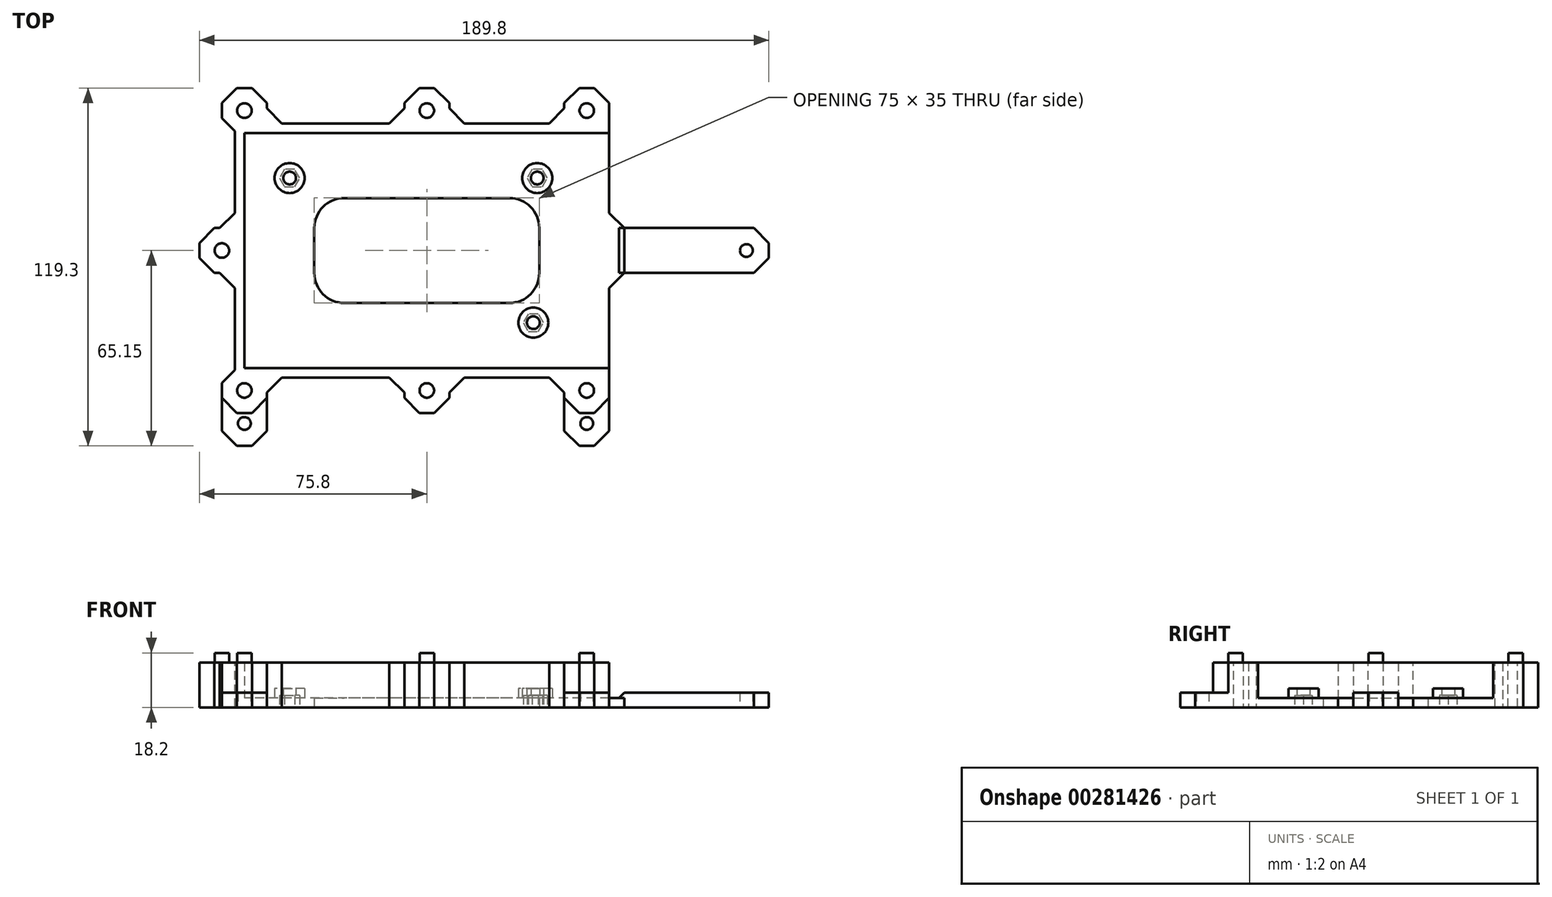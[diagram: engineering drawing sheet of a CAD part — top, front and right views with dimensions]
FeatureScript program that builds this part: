
annotation { "Feature Type Name" : "Feature", "Feature Type Description" : "" }
export const myFeature = defineFeature(function(context is Context, id is Id, definition is map)
    precondition{}
    {
        {
            var Q0;
            Q0=qCreatedBy(makeId("Top.planeOp"),FACE);
            var sketch = newSketch(context, id + "F0", { "sketchPlane" : qUnion([Q0])});
            skLineSegment(sketch, "E0.rect.bottom", {"start": v(50.8, -26.65) * mm, "end": v(-50.8, -26.65) * mm, "construction": true});
            skLineSegment(sketch, "E0.rect.top", {"start": v(50.8, 26.65) * mm, "end": v(-50.8, 26.65) * mm, "construction": true});
            skLineSegment(sketch, "E0.rect.left", {"start": v(50.8, -26.65) * mm, "end": v(50.8, 26.65) * mm, "construction": true});
            skLineSegment(sketch, "E0.rect.right", {"start": v(-50.8, -26.65) * mm, "end": v(-50.8, 26.65) * mm, "construction": true});
            skPoint(sketch, "E0.rect.middle", {"position": v(0, 0) * mm});
            skCircle(sketch, "E1", {"center": v(36.8, 24.15) * mm, "radius": 2.12 * mm});
            skCircle(sketch, "E2", {"center": v(-45.72, 24.15) * mm, "radius": 2.12 * mm});
            skLineSegment(sketch, "E3.rect.bottom", {"start": v(60.8, -39.15) * mm, "end": v(-60.8, -39.15) * mm});
            skLineSegment(sketch, "E3.rect.top", {"start": v(60.8, 39.15) * mm, "end": v(-60.8, 39.15) * mm});
            skLineSegment(sketch, "E3.rect.left", {"start": v(60.8, -39.15) * mm, "end": v(60.8, 39.15) * mm});
            skLineSegment(sketch, "E3.rect.right", {"start": v(-60.8, -39.15) * mm, "end": v(-60.8, 39.15) * mm});
            skLineSegment(sketch, "E4.rect.bottom", {"start": v(27.5, -17.5) * mm, "end": v(-27.5, -17.5) * mm});
            skLineSegment(sketch, "E4.rect.top", {"start": v(27.5, 17.5) * mm, "end": v(-27.5, 17.5) * mm});
            skLineSegment(sketch, "E4.rect.left", {"start": v(37.5, -7.5) * mm, "end": v(37.5, 7.5) * mm});
            skLineSegment(sketch, "E4.rect.right", {"start": v(-37.5, -7.5) * mm, "end": v(-37.5, 7.5) * mm});
            skPoint(sketch, "E5.visualSharp", {"position": v(-37.5, 17.5) * mm});
            skArc(sketch, "E5.filletArc", {"start": v(-27.5, 17.5) * mm, "mid": v(-34.57, 14.57) * mm, "end": v(-37.5, 7.5) * mm});
            skPoint(sketch, "E6.visualSharp", {"position": v(-37.5, -17.5) * mm});
            skArc(sketch, "E6.filletArc", {"start": v(-37.5, -7.5) * mm, "mid": v(-34.57, -14.57) * mm, "end": v(-27.5, -17.5) * mm});
            skPoint(sketch, "E7.visualSharp", {"position": v(37.5, -17.5) * mm});
            skArc(sketch, "E7.filletArc", {"start": v(27.5, -17.5) * mm, "mid": v(34.57, -14.57) * mm, "end": v(37.5, -7.5) * mm});
            skPoint(sketch, "E8.visualSharp", {"position": v(37.5, 17.5) * mm});
            skArc(sketch, "E8.filletArc", {"start": v(37.5, 7.5) * mm, "mid": v(34.57, 14.57) * mm, "end": v(27.5, 17.5) * mm});
            skCircle(sketch, "E9", {"center": v(35.5, -24.05) * mm, "radius": 2.12 * mm});
            skSolve(sketch);
        }
        {
            var Q0;
            Q0=qSketchRegion(id+"F0",true);
            extrude(context, id + "F1", {"entities" : qUnion([Q0]), "depth" : 3.2 * mm});
        }
        {
            var Q0;
            Q0=makeQuery(id+"F1.opExtrude","CAP_FACE",FACE,{"disambiguationData":[OSD([sQuery(id+"F0.wireOp",EDGE,"E1"),sQuery(id+"F0.wireOp",EDGE,"E2"),sQuery(id+"F0.wireOp",EDGE,"427397f8-0dd3-485f-8eed-9c75a59d67ec"),sQuery(id+"F0.wireOp",EDGE,"E3.rect.bottom"),sQuery(id+"F0.wireOp",EDGE,"E3.rect.top"),sQuery(id+"F0.wireOp",EDGE,"E3.rect.left"),sQuery(id+"F0.wireOp",EDGE,"E3.rect.right"),sQuery(id+"F0.wireOp",EDGE,"E4.rect.bottom"),sQuery(id+"F0.wireOp",EDGE,"E4.rect.top"),sQuery(id+"F0.wireOp",EDGE,"E4.rect.left"),sQuery(id+"F0.wireOp",EDGE,"E4.rect.right")])],"isStart":false});
            var sketch = newSketch(context, id + "F2", { "sketchPlane" : qUnion([Q0])});
            skCircle(sketch, "E10", {"center": v(-45.72, 24.15) * mm, "radius": 5 * mm});
            skCircle(sketch, "E11", {"center": v(36.8, 24.15) * mm, "radius": 5 * mm});
            skCircle(sketch, "E12", {"center": v(-45.72, 24.15) * mm, "radius": 2.12 * mm});
            skCircle(sketch, "E13", {"center": v(36.8, 24.15) * mm, "radius": 2.12 * mm});
            skLineSegment(sketch, "E14", {"start": v(0, 0) * mm, "end": v(17.05, 0) * mm, "construction": true});
            skCircle(sketch, "E15", {"center": v(35.5, -24.05) * mm, "radius": 5 * mm});
            skCircle(sketch, "E16", {"center": v(35.5, -24.05) * mm, "radius": 2.12 * mm});
            skSolve(sketch);
        }
        {
            var Q0;
            Q0=qSketchRegion(id+"F2",true);
            extrude(context, id + "F3", {"entities" : qUnion([Q0]), "operationType" : NewBodyOperationType.ADD, "depth" : 3.2 * mm});
        }
        {
            var Q0;
            Q0=makeQuery(id+"F1.opExtrude","CAP_FACE",FACE,{"disambiguationData":[OSD([sQuery(id+"F0.wireOp",EDGE,"E1"),sQuery(id+"F0.wireOp",EDGE,"E2"),sQuery(id+"F0.wireOp",EDGE,"427397f8-0dd3-485f-8eed-9c75a59d67ec"),sQuery(id+"F0.wireOp",EDGE,"E3.rect.bottom"),sQuery(id+"F0.wireOp",EDGE,"E3.rect.top"),sQuery(id+"F0.wireOp",EDGE,"E3.rect.left"),sQuery(id+"F0.wireOp",EDGE,"E3.rect.right"),sQuery(id+"F0.wireOp",EDGE,"E4.rect.bottom"),sQuery(id+"F0.wireOp",EDGE,"E4.rect.top"),sQuery(id+"F0.wireOp",EDGE,"E4.rect.left"),sQuery(id+"F0.wireOp",EDGE,"E4.rect.right")])],"isStart":true});
            var sketch = newSketch(context, id + "F4", { "sketchPlane" : qUnion([Q0])});
            skCircle(sketch, "E17.cCircle", {"center": v(-45.72, -24.15) * mm, "radius": 2.93 * mm, "construction": true});
            skLineSegment(sketch, "E17.0", {"start": v(-47.4, -21.23) * mm, "end": v(-44.03, -21.23) * mm});
            skLineSegment(sketch, "E17.1", {"start": v(-44.03, -21.23) * mm, "end": v(-42.34, -24.15) * mm});
            skLineSegment(sketch, "E17.2", {"start": v(-42.34, -24.15) * mm, "end": v(-44.03, -27.08) * mm});
            skLineSegment(sketch, "E17.3", {"start": v(-44.03, -27.08) * mm, "end": v(-47.4, -27.08) * mm});
            skLineSegment(sketch, "E17.4", {"start": v(-47.4, -27.08) * mm, "end": v(-49.1, -24.15) * mm});
            skLineSegment(sketch, "E17.5", {"start": v(-49.1, -24.15) * mm, "end": v(-47.4, -21.23) * mm});
            skPoint(sketch, "E17.0.midPoint", {"position": v(-45.72, -21.23) * mm});
            skCircle(sketch, "E18.cCircle", {"center": v(36.8, -24.15) * mm, "radius": 2.93 * mm, "construction": true});
            skLineSegment(sketch, "E18.0", {"start": v(35.11, -21.22) * mm, "end": v(38.49, -21.22) * mm});
            skLineSegment(sketch, "E18.1", {"start": v(38.49, -21.22) * mm, "end": v(40.18, -24.15) * mm});
            skLineSegment(sketch, "E18.2", {"start": v(40.18, -24.15) * mm, "end": v(38.49, -27.08) * mm});
            skLineSegment(sketch, "E18.3", {"start": v(38.49, -27.07) * mm, "end": v(35.11, -27.07) * mm});
            skLineSegment(sketch, "E18.4", {"start": v(35.11, -27.08) * mm, "end": v(33.42, -24.15) * mm});
            skLineSegment(sketch, "E18.5", {"start": v(33.42, -24.15) * mm, "end": v(35.11, -21.22) * mm});
            skPoint(sketch, "E18.0.midPoint", {"position": v(36.8, -21.23) * mm});
            skCircle(sketch, "E19.cCircle", {"center": v(35.5, 24.05) * mm, "radius": 2.93 * mm, "construction": true});
            skLineSegment(sketch, "E19.0", {"start": v(37.19, 21.12) * mm, "end": v(33.81, 21.12) * mm});
            skLineSegment(sketch, "E19.1", {"start": v(33.81, 21.12) * mm, "end": v(32.12, 24.05) * mm});
            skLineSegment(sketch, "E19.2", {"start": v(32.12, 24.05) * mm, "end": v(33.81, 26.97) * mm});
            skLineSegment(sketch, "E19.3", {"start": v(33.81, 26.97) * mm, "end": v(37.19, 26.97) * mm});
            skLineSegment(sketch, "E19.4", {"start": v(37.19, 26.97) * mm, "end": v(38.88, 24.05) * mm});
            skLineSegment(sketch, "E19.5", {"start": v(38.88, 24.05) * mm, "end": v(37.19, 21.12) * mm});
            skPoint(sketch, "E19.0.midPoint", {"position": v(35.5, 21.12) * mm});
            skSolve(sketch);
        }
        {
            var Q0;
            Q0=qSketchRegion(id+"F4",true);
            extrude(context, id + "F5", {"entities" : qUnion([Q0]), "operationType" : NewBodyOperationType.REMOVE, "oppositeDirection" : true, "depth" : 4 * mm});
        }
        {
            var Q0;
            Q0=qCreatedBy(makeId("Top.planeOp"),FACE);
            var sketch = newSketch(context, id + "F6", { "sketchPlane" : qUnion([Q0])});
            skLineSegment(sketch, "E20", {"start": v(60.8, 39.15) * mm, "end": v(-60.8, 39.15) * mm});
            skLineSegment(sketch, "E21", {"start": v(-60.8, 39.15) * mm, "end": v(-60.8, -39.15) * mm});
            skLineSegment(sketch, "E22", {"start": v(-60.8, -39.15) * mm, "end": v(60.8, -39.15) * mm});
            skLineSegment(sketch, "E23", {"start": v(60.8, -39.15) * mm, "end": v(60.8, -54.15) * mm});
            skLineSegment(sketch, "E24", {"start": v(60.8, -54.15) * mm, "end": v(45.8, -54.15) * mm});
            skLineSegment(sketch, "E25", {"start": v(45.8, -54.15) * mm, "end": v(45.8, -42.35) * mm});
            skLineSegment(sketch, "E26", {"start": v(45.8, -42.35) * mm, "end": v(7.5, -42.35) * mm});
            skLineSegment(sketch, "E27", {"start": v(7.5, -42.35) * mm, "end": v(7.5, -54.15) * mm});
            skLineSegment(sketch, "E28", {"start": v(7.5, -54.15) * mm, "end": v(-7.5, -54.15) * mm});
            skLineSegment(sketch, "E29", {"start": v(-7.5, -54.15) * mm, "end": v(-7.5, -42.35) * mm});
            skLineSegment(sketch, "E30", {"start": v(-7.5, -42.35) * mm, "end": v(-53.3, -42.35) * mm});
            skLineSegment(sketch, "E31", {"start": v(-53.3, -42.35) * mm, "end": v(-53.3, -54.15) * mm});
            skLineSegment(sketch, "E32", {"start": v(-53.3, -54.15) * mm, "end": v(-68.3, -54.15) * mm});
            skLineSegment(sketch, "E33", {"start": v(-68.3, -54.15) * mm, "end": v(-68.3, -39.15) * mm});
            skLineSegment(sketch, "E34", {"start": v(-68.3, -39.15) * mm, "end": v(-64, -39.15) * mm});
            skLineSegment(sketch, "E35", {"start": v(-64, -39.15) * mm, "end": v(-64, -7.5) * mm});
            skLineSegment(sketch, "E36", {"start": v(-64, -7.5) * mm, "end": v(-75.8, -7.5) * mm});
            skLineSegment(sketch, "E37", {"start": v(-75.8, -7.5) * mm, "end": v(-75.8, 7.5) * mm});
            skLineSegment(sketch, "E38", {"start": v(-75.8, 7.5) * mm, "end": v(-64, 7.5) * mm});
            skLineSegment(sketch, "E39", {"start": v(-64, 7.5) * mm, "end": v(-64, 39.15) * mm});
            skLineSegment(sketch, "E40", {"start": v(-64, 39.15) * mm, "end": v(-68.3, 39.15) * mm});
            skLineSegment(sketch, "E41", {"start": v(-68.3, 39.15) * mm, "end": v(-68.3, 54.15) * mm});
            skLineSegment(sketch, "E42", {"start": v(-68.3, 54.15) * mm, "end": v(-53.3, 54.15) * mm});
            skLineSegment(sketch, "E43", {"start": v(-53.3, 54.15) * mm, "end": v(-53.3, 42.35) * mm});
            skLineSegment(sketch, "E44", {"start": v(-53.3, 42.35) * mm, "end": v(-7.5, 42.35) * mm});
            skLineSegment(sketch, "E45", {"start": v(-7.5, 42.35) * mm, "end": v(-7.5, 54.15) * mm});
            skLineSegment(sketch, "E46", {"start": v(-7.5, 54.15) * mm, "end": v(7.5, 54.15) * mm});
            skLineSegment(sketch, "E47", {"start": v(7.5, 54.15) * mm, "end": v(7.5, 42.35) * mm});
            skLineSegment(sketch, "E48", {"start": v(7.5, 42.35) * mm, "end": v(45.8, 42.35) * mm});
            skLineSegment(sketch, "E49", {"start": v(45.8, 42.35) * mm, "end": v(45.8, 54.15) * mm});
            skLineSegment(sketch, "E50", {"start": v(45.8, 54.15) * mm, "end": v(60.8, 54.15) * mm});
            skLineSegment(sketch, "E51", {"start": v(60.8, 54.15) * mm, "end": v(60.8, 39.15) * mm});
            skSolve(sketch);
        }
        {
            var Q0;
            Q0=qSketchRegion(id+"F6",true);
            extrude(context, id + "F7", {"entities" : qUnion([Q0]), "operationType" : NewBodyOperationType.ADD, "depth" : 15 * mm});
        }
        {
            var Q0;
            Q0=makeQuery(id+"F7.opExtrude","CAP_FACE",FACE,{"disambiguationData":[OSD([sQuery(id+"F6.wireOp",EDGE,"E20"),sQuery(id+"F6.wireOp",EDGE,"E21"),sQuery(id+"F6.wireOp",EDGE,"E22"),sQuery(id+"F6.wireOp",EDGE,"E23"),sQuery(id+"F6.wireOp",EDGE,"E24"),sQuery(id+"F6.wireOp",EDGE,"E25"),sQuery(id+"F6.wireOp",EDGE,"E26"),sQuery(id+"F6.wireOp",EDGE,"E27"),sQuery(id+"F6.wireOp",EDGE,"E28"),sQuery(id+"F6.wireOp",EDGE,"E29"),sQuery(id+"F6.wireOp",EDGE,"E30"),sQuery(id+"F6.wireOp",EDGE,"E31"),sQuery(id+"F6.wireOp",EDGE,"E32"),sQuery(id+"F6.wireOp",EDGE,"E33"),sQuery(id+"F6.wireOp",EDGE,"E34"),sQuery(id+"F6.wireOp",EDGE,"E35"),sQuery(id+"F6.wireOp",EDGE,"E36"),sQuery(id+"F6.wireOp",EDGE,"E37"),sQuery(id+"F6.wireOp",EDGE,"E38"),sQuery(id+"F6.wireOp",EDGE,"E39"),sQuery(id+"F6.wireOp",EDGE,"E40"),sQuery(id+"F6.wireOp",EDGE,"E41"),sQuery(id+"F6.wireOp",EDGE,"E42"),sQuery(id+"F6.wireOp",EDGE,"E43"),sQuery(id+"F6.wireOp",EDGE,"E44"),sQuery(id+"F6.wireOp",EDGE,"E45"),sQuery(id+"F6.wireOp",EDGE,"E46"),sQuery(id+"F6.wireOp",EDGE,"E47"),sQuery(id+"F6.wireOp",EDGE,"E48"),sQuery(id+"F6.wireOp",EDGE,"E49"),sQuery(id+"F6.wireOp",EDGE,"E50"),sQuery(id+"F6.wireOp",EDGE,"E51")])],"isStart":false});
            var sketch = newSketch(context, id + "F8", { "sketchPlane" : qUnion([Q0])});
            skCircle(sketch, "E52", {"center": v(53.3, 46.65) * mm, "radius": 2.43 * mm});
            skCircle(sketch, "E53", {"center": v(0, 46.65) * mm, "radius": 2.43 * mm});
            skCircle(sketch, "E54", {"center": v(-60.8, 46.65) * mm, "radius": 2.43 * mm});
            skCircle(sketch, "E55", {"center": v(-68.3, 0) * mm, "radius": 2.43 * mm});
            skLineSegment(sketch, "E56", {"start": v(0, 0) * mm, "end": v(61.66, 0) * mm, "construction": true});
            skCircle(sketch, "E57.MirrorC", {"center": v(-60.8, -46.65) * mm, "radius": 2.43 * mm});
            skCircle(sketch, "E58.MirrorC", {"center": v(0, -46.65) * mm, "radius": 2.43 * mm});
            skCircle(sketch, "E59.MirrorC", {"center": v(53.3, -46.65) * mm, "radius": 2.43 * mm});
            skSolve(sketch);
        }
        {
            var Q0;
            Q0=qSketchRegion(id+"F8",true);
            extrude(context, id + "F9", {"entities" : qUnion([Q0]), "operationType" : NewBodyOperationType.ADD, "depth" : 3.2 * mm});
        }
        {
            var Q0;
            Q0=makeQuery(id+"F7.opExtrude","SWEPT_EDGE",EDGE,{"disambiguationData":[OSD([sQuery(id+"F6.wireOp",EDGE,"E36"),sQuery(id+"F6.wireOp",EDGE,"E37")])]});
            var Q1;
            Q1=makeQuery(id+"F7.opExtrude","SWEPT_EDGE",EDGE,{"disambiguationData":[OSD([sQuery(id+"F6.wireOp",EDGE,"E37"),sQuery(id+"F6.wireOp",EDGE,"E38")])]});
            var Q2;
            Q2=makeQuery(id+"F7.opExtrude","SWEPT_EDGE",EDGE,{"disambiguationData":[OSD([sQuery(id+"F6.wireOp",EDGE,"E41"),sQuery(id+"F6.wireOp",EDGE,"E42")])]});
            var Q3;
            Q3=makeQuery(id+"F7.opExtrude","SWEPT_EDGE",EDGE,{"disambiguationData":[OSD([sQuery(id+"F6.wireOp",EDGE,"E42"),sQuery(id+"F6.wireOp",EDGE,"E43")])]});
            var Q4;
            Q4=makeQuery(id+"F7.opExtrude","SWEPT_EDGE",EDGE,{"disambiguationData":[OSD([sQuery(id+"F6.wireOp",EDGE,"E45"),sQuery(id+"F6.wireOp",EDGE,"E46")])]});
            var Q5;
            Q5=makeQuery(id+"F7.opExtrude","SWEPT_EDGE",EDGE,{"disambiguationData":[OSD([sQuery(id+"F6.wireOp",EDGE,"E46"),sQuery(id+"F6.wireOp",EDGE,"E47")])]});
            var Q6;
            Q6=makeQuery(id+"F7.opExtrude","SWEPT_EDGE",EDGE,{"disambiguationData":[OSD([sQuery(id+"F6.wireOp",EDGE,"E49"),sQuery(id+"F6.wireOp",EDGE,"E50")])]});
            var Q7;
            Q7=makeQuery(id+"F7.opExtrude","SWEPT_EDGE",EDGE,{"disambiguationData":[OSD([sQuery(id+"F6.wireOp",EDGE,"E50"),sQuery(id+"F6.wireOp",EDGE,"E51")])]});
            var Q8;
            Q8=makeQuery(id+"F7.opExtrude","SWEPT_EDGE",EDGE,{"disambiguationData":[OSD([sQuery(id+"F6.wireOp",EDGE,"E23"),sQuery(id+"F6.wireOp",EDGE,"E24")])]});
            var Q9;
            Q9=makeQuery(id+"F7.opExtrude","SWEPT_EDGE",EDGE,{"disambiguationData":[OSD([sQuery(id+"F6.wireOp",EDGE,"E24"),sQuery(id+"F6.wireOp",EDGE,"E25")])]});
            var Q10;
            Q10=makeQuery(id+"F7.opExtrude","SWEPT_EDGE",EDGE,{"disambiguationData":[OSD([sQuery(id+"F6.wireOp",EDGE,"E27"),sQuery(id+"F6.wireOp",EDGE,"E28")])]});
            var Q11;
            Q11=makeQuery(id+"F7.opExtrude","SWEPT_EDGE",EDGE,{"disambiguationData":[OSD([sQuery(id+"F6.wireOp",EDGE,"E28"),sQuery(id+"F6.wireOp",EDGE,"E29")])]});
            var Q12;
            Q12=makeQuery(id+"F7.opExtrude","SWEPT_EDGE",EDGE,{"disambiguationData":[OSD([sQuery(id+"F6.wireOp",EDGE,"E31"),sQuery(id+"F6.wireOp",EDGE,"E32")])]});
            var Q13;
            Q13=makeQuery(id+"F7.opExtrude","SWEPT_EDGE",EDGE,{"disambiguationData":[OSD([sQuery(id+"F6.wireOp",EDGE,"E32"),sQuery(id+"F6.wireOp",EDGE,"E33")])]});
            var Q14;
            Q14=makeQuery(id+"F7.opExtrude","SWEPT_EDGE",EDGE,{"disambiguationData":[OSD([sQuery(id+"F6.wireOp",EDGE,"E40"),sQuery(id+"F6.wireOp",EDGE,"E41")])]});
            var Q15;
            Q15=makeQuery(id+"F7.opExtrude","SWEPT_EDGE",EDGE,{"disambiguationData":[OSD([sQuery(id+"F6.wireOp",EDGE,"E33"),sQuery(id+"F6.wireOp",EDGE,"E34")])]});
            var Q16;
            Q16=makeQuery(id+"F7.opExtrude","SWEPT_EDGE",EDGE,{"disambiguationData":[OSD([sQuery(id+"F6.wireOp",EDGE,"E29"),sQuery(id+"F6.wireOp",EDGE,"E30")])]});
            var Q17;
            Q17=makeQuery(id+"F7.opExtrude","SWEPT_EDGE",EDGE,{"disambiguationData":[OSD([sQuery(id+"F6.wireOp",EDGE,"E26"),sQuery(id+"F6.wireOp",EDGE,"E27")])]});
            var Q18;
            Q18=makeQuery(id+"F7.opExtrude","SWEPT_EDGE",EDGE,{"disambiguationData":[OSD([sQuery(id+"F6.wireOp",EDGE,"E25"),sQuery(id+"F6.wireOp",EDGE,"E26")])]});
            var Q19;
            Q19=makeQuery(id+"F7.opExtrude","SWEPT_EDGE",EDGE,{"disambiguationData":[OSD([sQuery(id+"F6.wireOp",EDGE,"E30"),sQuery(id+"F6.wireOp",EDGE,"E31")])]});
            var Q20;
            Q20=makeQuery(id+"F7.opExtrude","SWEPT_EDGE",EDGE,{"disambiguationData":[OSD([sQuery(id+"F6.wireOp",EDGE,"E35"),sQuery(id+"F6.wireOp",EDGE,"E36")])]});
            var Q21;
            Q21=makeQuery(id+"F7.opExtrude","SWEPT_EDGE",EDGE,{"disambiguationData":[OSD([sQuery(id+"F6.wireOp",EDGE,"E38"),sQuery(id+"F6.wireOp",EDGE,"E39")])]});
            var Q22;
            Q22=makeQuery(id+"F7.opExtrude","SWEPT_EDGE",EDGE,{"disambiguationData":[OSD([sQuery(id+"F6.wireOp",EDGE,"E43"),sQuery(id+"F6.wireOp",EDGE,"E44")])]});
            var Q23;
            Q23=makeQuery(id+"F7.opExtrude","SWEPT_EDGE",EDGE,{"disambiguationData":[OSD([sQuery(id+"F6.wireOp",EDGE,"E44"),sQuery(id+"F6.wireOp",EDGE,"E45")])]});
            var Q24;
            Q24=makeQuery(id+"F7.opExtrude","SWEPT_EDGE",EDGE,{"disambiguationData":[OSD([sQuery(id+"F6.wireOp",EDGE,"E48"),sQuery(id+"F6.wireOp",EDGE,"E49")])]});
            var Q25;
            Q25=makeQuery(id+"F7.opExtrude","SWEPT_EDGE",EDGE,{"disambiguationData":[OSD([sQuery(id+"F6.wireOp",EDGE,"E47"),sQuery(id+"F6.wireOp",EDGE,"E48")])]});
            chamfer(context, id + "F10", {"entities" : qUnion([Q0, Q1, Q2, Q3, Q4, Q5, Q6, Q7, Q8, Q9, Q10, Q11, Q12, Q13, Q14, Q15, Q16, Q17, Q18, Q19, Q20, Q21, Q22, Q23, Q24, Q25]), "width" : 5 * mm, "tangentPropagation" : true});
        }
        {
            var Q0;
            Q0=qCreatedBy(makeId("Top.planeOp"),FACE);
            var sketch = newSketch(context, id + "F11", { "sketchPlane" : qUnion([Q0])});
            skLineSegment(sketch, "E60.bottom", {"start": v(-53.3, 47.35) * mm, "end": v(-68.3, 47.35) * mm, "construction": true});
            skLineSegment(sketch, "E60.top", {"start": v(-53.3, 65.15) * mm, "end": v(-68.3, 65.15) * mm, "construction": true});
            skLineSegment(sketch, "E60.left", {"start": v(-53.3, 47.35) * mm, "end": v(-53.3, 65.15) * mm, "construction": true});
            skLineSegment(sketch, "E60.right", {"start": v(-68.3, 47.35) * mm, "end": v(-68.3, 65.15) * mm, "construction": true});
            skPoint(sketch, "E60.middle", {"position": v(-60.8, 56.25) * mm});
            skCircle(sketch, "E61", {"center": v(-60.8, 57.65) * mm, "radius": 2.12 * mm, "construction": true});
            skLineSegment(sketch, "E62.bottom", {"start": v(60.8, 47.35) * mm, "end": v(45.8, 47.35) * mm, "construction": true});
            skLineSegment(sketch, "E62.top", {"start": v(60.8, 65.15) * mm, "end": v(45.8, 65.15) * mm, "construction": true});
            skLineSegment(sketch, "E62.left", {"start": v(60.8, 47.35) * mm, "end": v(60.8, 65.15) * mm, "construction": true});
            skLineSegment(sketch, "E62.right", {"start": v(45.8, 47.35) * mm, "end": v(45.8, 65.15) * mm, "construction": true});
            skPoint(sketch, "E62.middle", {"position": v(53.3, 56.25) * mm});
            skCircle(sketch, "E63", {"center": v(53.3, 57.65) * mm, "radius": 2.12 * mm, "construction": true});
            skLineSegment(sketch, "E64", {"start": v(0, 0) * mm, "end": v(61.36, 0) * mm, "construction": true});
            skCircle(sketch, "E65", {"center": v(-60.8, 57.65) * mm, "radius": 3.25 * mm, "construction": true});
            skCircle(sketch, "E66.MirrorC", {"center": v(-60.8, -57.65) * mm, "radius": 2.12 * mm});
            skLineSegment(sketch, "E67.MirrorCS", {"start": v(60.8, -65.15) * mm, "end": v(45.8, -65.15) * mm});
            skLineSegment(sketch, "E68.MirrorCS", {"start": v(-53.3, -65.15) * mm, "end": v(-68.3, -65.15) * mm});
            skCircle(sketch, "E69.MirrorC", {"center": v(53.3, -57.65) * mm, "radius": 2.12 * mm});
            skCircle(sketch, "E70.MirrorC", {"center": v(-60.8, -57.65) * mm, "radius": 3.25 * mm, "construction": true});
            skPoint(sketch, "E71.MirrorP", {"position": v(53.3, -56.25) * mm});
            skPoint(sketch, "E72.MirrorP", {"position": v(-60.8, -56.25) * mm});
            skLineSegment(sketch, "E73.MirrorCS", {"start": v(60.8, -47.35) * mm, "end": v(60.8, -65.15) * mm});
            skLineSegment(sketch, "E74.MirrorCS", {"start": v(45.8, -47.35) * mm, "end": v(45.8, -65.15) * mm});
            skLineSegment(sketch, "E75.MirrorCS", {"start": v(-53.3, -47.35) * mm, "end": v(-53.3, -65.15) * mm});
            skLineSegment(sketch, "E76.MirrorCS", {"start": v(-68.3, -47.35) * mm, "end": v(-68.3, -65.15) * mm});
            skLineSegment(sketch, "E77.MirrorCS", {"start": v(60.8, -47.35) * mm, "end": v(45.8, -47.35) * mm});
            skLineSegment(sketch, "E78.MirrorCS", {"start": v(-53.3, -47.35) * mm, "end": v(-68.3, -47.35) * mm});
            skLineSegment(sketch, "E79.bottom", {"start": v(-63.23, 34.15) * mm, "end": v(-118.23, 34.15) * mm, "construction": true});
            skLineSegment(sketch, "E79.top", {"start": v(-63.23, 54.15) * mm, "end": v(-118.23, 54.15) * mm, "construction": true});
            skLineSegment(sketch, "E79.left", {"start": v(-63.23, 34.15) * mm, "end": v(-63.23, 54.15) * mm, "construction": true});
            skLineSegment(sketch, "E79.right", {"start": v(-118.23, 34.15) * mm, "end": v(-118.23, 54.15) * mm, "construction": true});
            skCircle(sketch, "E80", {"center": v(-110.73, 44.15) * mm, "radius": 2.12 * mm, "construction": true});
            skLineSegment(sketch, "E81.bottom", {"start": v(-64, 7.5) * mm, "end": v(-114, 7.5) * mm, "construction": true});
            skLineSegment(sketch, "E81.top", {"start": v(-64, -7.5) * mm, "end": v(-114, -7.5) * mm, "construction": true});
            skLineSegment(sketch, "E81.left", {"start": v(-64, 7.5) * mm, "end": v(-64, -7.5) * mm, "construction": true});
            skLineSegment(sketch, "E81.right", {"start": v(-114, 7.5) * mm, "end": v(-114, -7.5) * mm, "construction": true});
            skCircle(sketch, "E82", {"center": v(-106.5, 0) * mm, "radius": 2.12 * mm, "construction": true});
            skLineSegment(sketch, "E83.MirrorCS", {"start": v(64, -7.5) * mm, "end": v(114, -7.5) * mm});
            skLineSegment(sketch, "E84.MirrorCS", {"start": v(64, 7.5) * mm, "end": v(114, 7.5) * mm});
            skLineSegment(sketch, "E85.MirrorCS", {"start": v(114, 7.5) * mm, "end": v(114, -7.5) * mm});
            skCircle(sketch, "E86.MirrorC", {"center": v(106.5, 0) * mm, "radius": 2.12 * mm});
            skLineSegment(sketch, "E87.MirrorCS", {"start": v(64, 7.5) * mm, "end": v(64, -7.5) * mm, "construction": true});
            skLineSegment(sketch, "E88", {"start": v(64, 7.5) * mm, "end": v(60.8, 7.5) * mm});
            skLineSegment(sketch, "E89", {"start": v(64, -7.5) * mm, "end": v(60.8, -7.5) * mm});
            skLineSegment(sketch, "E90", {"start": v(60.8, -7.5) * mm, "end": v(60.8, 7.5) * mm});
            skSolve(sketch);
        }
        {
            var Q0;
            Q0=qSketchRegion(id+"F11",true);
            extrude(context, id + "F12", {"entities" : qUnion([Q0]), "operationType" : NewBodyOperationType.ADD, "depth" : 5 * mm});
        }
        {
            var Q0;
            {var subQ19=sQuery(id+"F11.wireOp",EDGE,"eqWCjPbX-htDR-C8ga-Of8s-fPPzDfkzrk7Z.right");var subQ20=sQuery(id+"F11.wireOp",EDGE,"eqWCjPbX-htDR-C8ga-Of8s-fPPzDfkzrk7Z.top");Q0=makeQuery(id+"F12.boolean.opBoolean","SPLIT",EDGE,{"disambiguationData":[TD([makeQuery(id+"F12.opExtrude","CAP_FACE",FACE,{"disambiguationData":[OSD([sQuery(id+"F11.wireOp",EDGE,"jk3RAOnG-DA1z-41IM-KuVU-WPvvxcmoacko.bottom"),sQuery(id+"F11.wireOp",EDGE,"jk3RAOnG-DA1z-41IM-KuVU-WPvvxcmoacko.top"),sQuery(id+"F11.wireOp",EDGE,"jk3RAOnG-DA1z-41IM-KuVU-WPvvxcmoacko.left"),sQuery(id+"F11.wireOp",EDGE,"jk3RAOnG-DA1z-41IM-KuVU-WPvvxcmoacko.right"),sQuery(id+"F11.wireOp",EDGE,"J50HAIJv-iOe3-t8LS-iFIo-mBBWgSaYphRW")])],"isStart":true})])],"derivedFrom":makeQuery(id+"F12.opExtrude","SWEPT_EDGE",EDGE,{"disambiguationData":[OSD([subQ20,subQ19])]})});}
            var Q1;
            Q1=makeQuery(id+"F12.opExtrude","SWEPT_EDGE",EDGE,{"disambiguationData":[OSD([sQuery(id+"F11.wireOp",EDGE,"eqWCjPbX-htDR-C8ga-Of8s-fPPzDfkzrk7Z.top"),sQuery(id+"F11.wireOp",EDGE,"eqWCjPbX-htDR-C8ga-Of8s-fPPzDfkzrk7Z.left")])]});
            var Q2;
            Q2=makeQuery(id+"F12.opExtrude","SWEPT_EDGE",EDGE,{"disambiguationData":[OSD([sQuery(id+"F11.wireOp",EDGE,"eqWCjPbX-htDR-C8ga-Of8s-fPPzDfkzrk7Z.bottom"),sQuery(id+"F11.wireOp",EDGE,"eqWCjPbX-htDR-C8ga-Of8s-fPPzDfkzrk7Z.left")])]});
            var Q3;
            {var subQ18=sQuery(id+"F11.wireOp",EDGE,"eqWCjPbX-htDR-C8ga-Of8s-fPPzDfkzrk7Z.bottom");var subQ20=sQuery(id+"F11.wireOp",EDGE,"eqWCjPbX-htDR-C8ga-Of8s-fPPzDfkzrk7Z.right");Q3=makeQuery(id+"F12.boolean.opBoolean","SPLIT",EDGE,{"disambiguationData":[TD([makeQuery(id+"F12.opExtrude","CAP_FACE",FACE,{"disambiguationData":[OSD([sQuery(id+"F11.wireOp",EDGE,"jk3RAOnG-DA1z-41IM-KuVU-WPvvxcmoacko.bottom"),sQuery(id+"F11.wireOp",EDGE,"jk3RAOnG-DA1z-41IM-KuVU-WPvvxcmoacko.top"),sQuery(id+"F11.wireOp",EDGE,"jk3RAOnG-DA1z-41IM-KuVU-WPvvxcmoacko.left"),sQuery(id+"F11.wireOp",EDGE,"jk3RAOnG-DA1z-41IM-KuVU-WPvvxcmoacko.right"),sQuery(id+"F11.wireOp",EDGE,"J50HAIJv-iOe3-t8LS-iFIo-mBBWgSaYphRW")])],"isStart":true})])],"derivedFrom":makeQuery(id+"F12.opExtrude","SWEPT_EDGE",EDGE,{"disambiguationData":[OSD([subQ18,subQ20])]})});}
            var Q4;
            Q4=makeQuery(id+"F12.opExtrude","SWEPT_EDGE",EDGE,{"disambiguationData":[OSD([sQuery(id+"F11.wireOp",EDGE,"E62.top"),sQuery(id+"F11.wireOp",EDGE,"E62.left")])]});
            var Q5;
            Q5=makeQuery(id+"F12.opExtrude","SWEPT_EDGE",EDGE,{"disambiguationData":[OSD([sQuery(id+"F11.wireOp",EDGE,"E62.top"),sQuery(id+"F11.wireOp",EDGE,"E62.right")])]});
            var Q6;
            Q6=makeQuery(id+"F12.opExtrude","SWEPT_EDGE",EDGE,{"disambiguationData":[OSD([sQuery(id+"F11.wireOp",EDGE,"jk3RAOnG-DA1z-41IM-KuVU-WPvvxcmoacko.top"),sQuery(id+"F11.wireOp",EDGE,"jk3RAOnG-DA1z-41IM-KuVU-WPvvxcmoacko.left")])]});
            var Q7;
            Q7=makeQuery(id+"F12.opExtrude","SWEPT_EDGE",EDGE,{"disambiguationData":[OSD([sQuery(id+"F11.wireOp",EDGE,"jk3RAOnG-DA1z-41IM-KuVU-WPvvxcmoacko.top"),sQuery(id+"F11.wireOp",EDGE,"jk3RAOnG-DA1z-41IM-KuVU-WPvvxcmoacko.right")])]});
            var Q8;
            Q8=makeQuery(id+"F12.opExtrude","SWEPT_EDGE",EDGE,{"disambiguationData":[OSD([sQuery(id+"F11.wireOp",EDGE,"E60.top"),sQuery(id+"F11.wireOp",EDGE,"E60.right")])]});
            var Q9;
            Q9=makeQuery(id+"F12.opExtrude","SWEPT_EDGE",EDGE,{"disambiguationData":[OSD([sQuery(id+"F11.wireOp",EDGE,"E60.top"),sQuery(id+"F11.wireOp",EDGE,"E60.left")])]});
            var Q10;
            Q10=makeQuery(id+"F12.opExtrude","SWEPT_EDGE",EDGE,{"disambiguationData":[OSD([sQuery(id+"F11.wireOp",EDGE,"7W6G90EH-0ySu-CVKN-ljKH-nmCfsKCbzxSo.top"),sQuery(id+"F11.wireOp",EDGE,"7W6G90EH-0ySu-CVKN-ljKH-nmCfsKCbzxSo.right")])]});
            var Q11;
            Q11=makeQuery(id+"F12.opExtrude","SWEPT_EDGE",EDGE,{"disambiguationData":[OSD([sQuery(id+"F11.wireOp",EDGE,"7W6G90EH-0ySu-CVKN-ljKH-nmCfsKCbzxSo.bottom"),sQuery(id+"F11.wireOp",EDGE,"7W6G90EH-0ySu-CVKN-ljKH-nmCfsKCbzxSo.right")])]});
            var Q12;
            Q12=makeQuery(id+"F12.opExtrude","SWEPT_EDGE",EDGE,{"disambiguationData":[OSD([sQuery(id+"F11.wireOp",EDGE,"963d92d2-a4c7-402a-b001-3de9b50f85252.MirrorCS"),sQuery(id+"F11.wireOp",EDGE,"963d92d2-a4c7-402a-b001-3de9b50f85257.MirrorCS")])]});
            var Q13;
            Q13=makeQuery(id+"F12.opExtrude","SWEPT_EDGE",EDGE,{"disambiguationData":[OSD([sQuery(id+"F11.wireOp",EDGE,"963d92d2-a4c7-402a-b001-3de9b50f85252.MirrorCS"),sQuery(id+"F11.wireOp",EDGE,"963d92d2-a4c7-402a-b001-3de9b50f85258.MirrorCS")])]});
            var Q14;
            Q14=makeQuery(id+"F12.opExtrude","SWEPT_EDGE",EDGE,{"disambiguationData":[OSD([sQuery(id+"F11.wireOp",EDGE,"963d92d2-a4c7-402a-b001-3de9b50f852516.MirrorCS"),sQuery(id+"F11.wireOp",EDGE,"963d92d2-a4c7-402a-b001-3de9b50f852517.MirrorCS")])]});
            var Q15;
            Q15=makeQuery(id+"F12.opExtrude","SWEPT_EDGE",EDGE,{"disambiguationData":[OSD([sQuery(id+"F11.wireOp",EDGE,"963d92d2-a4c7-402a-b001-3de9b50f852513.MirrorCS"),sQuery(id+"F11.wireOp",EDGE,"963d92d2-a4c7-402a-b001-3de9b50f852516.MirrorCS")])]});
            var Q16;
            Q16=makeQuery(id+"F12.opExtrude","SWEPT_EDGE",EDGE,{"disambiguationData":[OSD([sQuery(id+"F11.wireOp",EDGE,"963d92d2-a4c7-402a-b001-3de9b50f85255.MirrorCS"),sQuery(id+"F11.wireOp",EDGE,"963d92d2-a4c7-402a-b001-3de9b50f852510.MirrorCS")])]});
            var Q17;
            Q17=makeQuery(id+"F12.opExtrude","SWEPT_EDGE",EDGE,{"disambiguationData":[OSD([sQuery(id+"F11.wireOp",EDGE,"963d92d2-a4c7-402a-b001-3de9b50f852510.MirrorCS"),sQuery(id+"F11.wireOp",EDGE,"963d92d2-a4c7-402a-b001-3de9b50f852512.MirrorCS")])]});
            var Q18;
            {var subQ0=sQuery(id+"F6.wireOp",EDGE,"E35");Q18=makeQuery(id+"F12.boolean.opBoolean","MERGE",EDGE,{"derivedFrom":[makeQuery(id+"F10.opChamfer","BLEND_EDGE",EDGE,{"blendedFrom":[makeQuery(id+"F7.opExtrude","SWEPT_EDGE",EDGE,{"disambiguationData":[OSD([subQ0,sQuery(id+"F6.wireOp",EDGE,"E36")])]}),makeQuery(id+"F7.opExtrude","SWEPT_FACE",FACE,{"disambiguationData":[OSD([subQ0])]})],"blendedInto":[makeQuery(id+"F7.opExtrude","SWEPT_FACE",FACE,{"disambiguationData":[OSD([subQ0])]})]}),makeQuery(id+"F12.opExtrude","SWEPT_EDGE",EDGE,{"disambiguationData":[OSD([sQuery(id+"F11.wireOp",EDGE,"7W6G90EH-0ySu-CVKN-ljKH-nmCfsKCbzxSo.bottom"),sQuery(id+"F11.wireOp",EDGE,"7W6G90EH-0ySu-CVKN-ljKH-nmCfsKCbzxSo.left")])]})]});}
            var Q19;
            {var subQ0=sQuery(id+"F6.wireOp",EDGE,"E39");Q19=makeQuery(id+"F12.boolean.opBoolean","MERGE",EDGE,{"derivedFrom":[makeQuery(id+"F10.opChamfer","BLEND_EDGE",EDGE,{"blendedFrom":[makeQuery(id+"F7.opExtrude","SWEPT_EDGE",EDGE,{"disambiguationData":[OSD([sQuery(id+"F6.wireOp",EDGE,"E38"),subQ0])]}),makeQuery(id+"F7.opExtrude","SWEPT_FACE",FACE,{"disambiguationData":[OSD([subQ0])]})],"blendedInto":[makeQuery(id+"F7.opExtrude","SWEPT_FACE",FACE,{"disambiguationData":[OSD([subQ0])]})]}),makeQuery(id+"F12.opExtrude","SWEPT_EDGE",EDGE,{"disambiguationData":[OSD([sQuery(id+"F11.wireOp",EDGE,"7W6G90EH-0ySu-CVKN-ljKH-nmCfsKCbzxSo.top"),sQuery(id+"F11.wireOp",EDGE,"7W6G90EH-0ySu-CVKN-ljKH-nmCfsKCbzxSo.left")])]})]});}
            var Q20;
            Q20=makeQuery(id+"F12.opExtrude","SWEPT_EDGE",EDGE,{"disambiguationData":[OSD([sQuery(id+"F11.wireOp",EDGE,"E68.MirrorCS"),sQuery(id+"F11.wireOp",EDGE,"E76.MirrorCS")])]});
            var Q21;
            Q21=makeQuery(id+"F12.opExtrude","SWEPT_EDGE",EDGE,{"disambiguationData":[OSD([sQuery(id+"F11.wireOp",EDGE,"E68.MirrorCS"),sQuery(id+"F11.wireOp",EDGE,"E75.MirrorCS")])]});
            var Q22;
            Q22=makeQuery(id+"F12.opExtrude","SWEPT_EDGE",EDGE,{"disambiguationData":[OSD([sQuery(id+"F11.wireOp",EDGE,"E67.MirrorCS"),sQuery(id+"F11.wireOp",EDGE,"E74.MirrorCS")])]});
            var Q23;
            Q23=makeQuery(id+"F12.opExtrude","SWEPT_EDGE",EDGE,{"disambiguationData":[OSD([sQuery(id+"F11.wireOp",EDGE,"E67.MirrorCS"),sQuery(id+"F11.wireOp",EDGE,"E73.MirrorCS")])]});
            var Q24;
            Q24=makeQuery(id+"F12.opExtrude","SWEPT_EDGE",EDGE,{"disambiguationData":[OSD([sQuery(id+"F11.wireOp",EDGE,"E79.top"),sQuery(id+"F11.wireOp",EDGE,"E79.right")])]});
            var Q25;
            Q25=makeQuery(id+"F12.opExtrude","SWEPT_EDGE",EDGE,{"disambiguationData":[OSD([sQuery(id+"F11.wireOp",EDGE,"E79.bottom"),sQuery(id+"F11.wireOp",EDGE,"E79.right")])]});
            var Q26;
            Q26=makeQuery(id+"F12.boolean.opBoolean","INTERSECT",EDGE,{"derivedFrom":[makeQuery(id+"F7.opExtrude","SWEPT_FACE",FACE,{"disambiguationData":[OSD([sQuery(id+"F6.wireOp",EDGE,"E39")])]}),makeQuery(id+"F12.opExtrude","SWEPT_FACE",FACE,{"disambiguationData":[OSD([sQuery(id+"F11.wireOp",EDGE,"E79.bottom")])]})]});
            var Q27;
            Q27=makeQuery(id+"F12.opExtrude","SWEPT_EDGE",EDGE,{"disambiguationData":[OSD([sQuery(id+"F11.wireOp",EDGE,"E81.bottom"),sQuery(id+"F11.wireOp",EDGE,"E81.right")])]});
            var Q28;
            Q28=makeQuery(id+"F12.opExtrude","SWEPT_EDGE",EDGE,{"disambiguationData":[OSD([sQuery(id+"F11.wireOp",EDGE,"E81.top"),sQuery(id+"F11.wireOp",EDGE,"E81.right")])]});
            var Q29;
            Q29=makeQuery(id+"F12.opExtrude","SWEPT_EDGE",EDGE,{"disambiguationData":[OSD([sQuery(id+"F11.wireOp",EDGE,"E84.MirrorCS"),sQuery(id+"F11.wireOp",EDGE,"E85.MirrorCS")])]});
            var Q30;
            Q30=makeQuery(id+"F12.opExtrude","SWEPT_EDGE",EDGE,{"disambiguationData":[OSD([sQuery(id+"F11.wireOp",EDGE,"E83.MirrorCS"),sQuery(id+"F11.wireOp",EDGE,"E85.MirrorCS")])]});
            var Q31;
            {var subQ0=sQuery(id+"F11.wireOp",EDGE,"E88");Q31=makeQuery(id+"F12.boolean.opBoolean","SPLIT",EDGE,{"disambiguationData":[topologyDisambiguationEdgeConnected([makeQuery(id+"F1.opExtrude","SWEPT_FACE",FACE,{"disambiguationData":[OSD([sQuery(id+"F0.wireOp",EDGE,"E3.rect.left")])]})])],"derivedFrom":makeQuery(id+"F12.opExtrude","SWEPT_EDGE",EDGE,{"disambiguationData":[OSD([subQ0,sQuery(id+"F11.wireOp",EDGE,"E90")])]})});}
            var Q32;
            {var subQ0=sQuery(id+"F11.wireOp",EDGE,"E89");Q32=makeQuery(id+"F12.boolean.opBoolean","SPLIT",EDGE,{"disambiguationData":[topologyDisambiguationEdgeConnected([makeQuery(id+"F1.opExtrude","SWEPT_FACE",FACE,{"disambiguationData":[OSD([sQuery(id+"F0.wireOp",EDGE,"E3.rect.left")])]})])],"derivedFrom":makeQuery(id+"F12.opExtrude","SWEPT_EDGE",EDGE,{"disambiguationData":[OSD([subQ0,sQuery(id+"F11.wireOp",EDGE,"E90")])]})});}
            chamfer(context, id + "F13", {"entities" : qUnion([Q0, Q1, Q2, Q3, Q4, Q5, Q6, Q7, Q8, Q9, Q10, Q11, Q12, Q13, Q14, Q15, Q16, Q17, Q18, Q19, Q20, Q21, Q22, Q23, Q24, Q25, Q26, Q27, Q28, Q29, Q30, Q31, Q32]), "width" : 5 * mm, "tangentPropagation" : true});
        }
        {
            var Q0;
            Q0=makeQuery(id+"F12.opExtrude","CAP_EDGE",EDGE,{"disambiguationData":[OSD([sQuery(id+"F11.wireOp",EDGE,"E90")])],"isStart":false});
            chamfer(context, id + "F14", {"entities" : qUnion([Q0]), "width" : 5 * mm, "tangentPropagation" : true});
        }
    });
